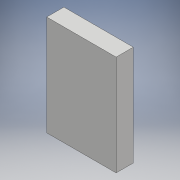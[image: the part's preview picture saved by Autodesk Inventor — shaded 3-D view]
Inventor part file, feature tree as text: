
AUTODESK INVENTOR PART (.ipt)
format: ipt  version: 2017 (Build 210142000, 142)  size: 88,064 bytes
history: native  units: mm
features: extrude x1, sketch x1
ambient origin geometry x8: Origin, YZ Plane, XZ Plane, XY Plane, X Axis, Y Axis, Z Axis, Center Point
bodies: Solid1 (feature_tree)
feature tree (2):
  extrude  "Extrusion1"  Depth=25.0mm
  sketch  "Sketch1"  dims[d0=101.0mm d1=25.0mm d2=146.0mm d3=0.0mm]
